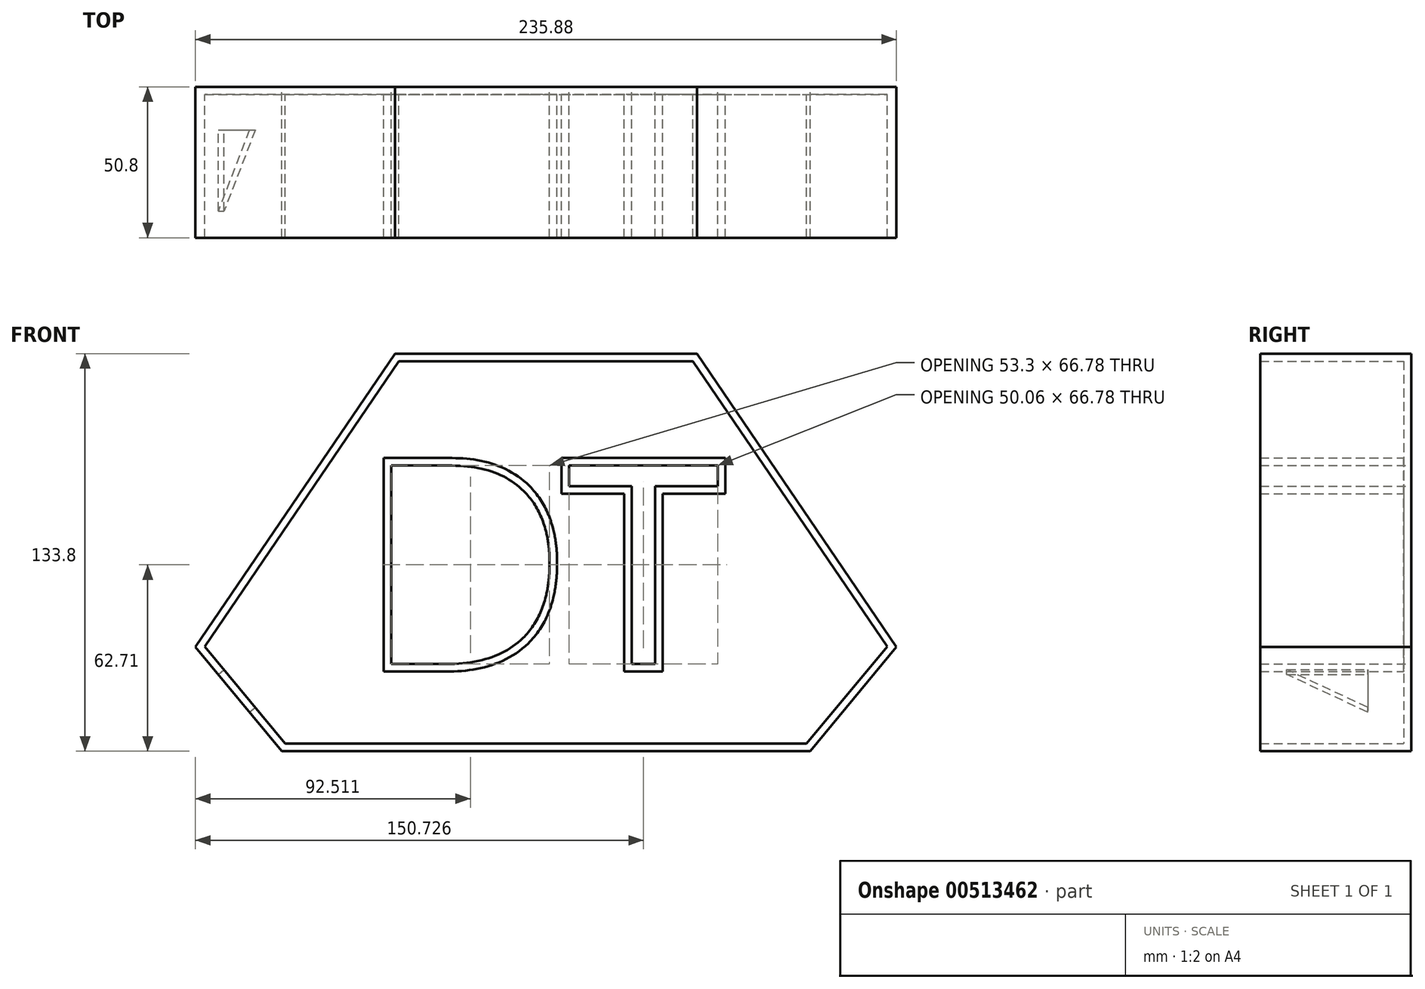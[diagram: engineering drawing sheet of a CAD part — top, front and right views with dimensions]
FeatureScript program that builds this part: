
annotation { "Feature Type Name" : "Feature", "Feature Type Description" : "" }
export const myFeature = defineFeature(function(context is Context, id is Id, definition is map)
    precondition{}
    {
        {
            var Q0;
            Q0=qCreatedBy(makeId("Front.planeOp"),FACE);
            var sketch = newSketch(context, id + "F0", { "sketchPlane" : qUnion([Q0])});
            skPoint(sketch, "E0.visualSharp", {"position": v(60.06, -91.32) * mm});
            skLineSegment(sketch, "E1", {"start": v(0, 83.88) * mm, "end": v(-50.8, 83.88) * mm});
            skLineSegment(sketch, "E2", {"start": v(-50.8, 83.88) * mm, "end": v(-117.94, -14.83) * mm});
            skLineSegment(sketch, "E3", {"start": v(-117.94, -14.83) * mm, "end": v(-88.9, -49.92) * mm});
            skLineSegment(sketch, "E4", {"start": v(-88.9, -49.92) * mm, "end": v(0, -49.92) * mm});
            skLineSegment(sketch, "E5.MirrorCS", {"start": v(0, 83.88) * mm, "end": v(50.8, 83.88) * mm});
            skLineSegment(sketch, "E6.MirrorCS", {"start": v(50.8, 83.88) * mm, "end": v(117.94, -14.83) * mm});
            skLineSegment(sketch, "E7.MirrorCS", {"start": v(117.94, -14.83) * mm, "end": v(88.9, -49.92) * mm});
            skLineSegment(sketch, "E8.MirrorCS", {"start": v(88.9, -49.92) * mm, "end": v(0, -49.92) * mm});
            skLineSegment(sketch, "E9", {"start": v(0, 83.88) * mm, "end": v(0, -49.92) * mm});
            skPoint(sketch, "E10.start.orphan", {"position": v(30.5, 62.6) * mm});
            skPoint(sketch, "E11.orphan", {"position": v(11.21, 62.6) * mm});
            skPoint(sketch, "E12.end.orphan", {"position": v(49.78, 62.6) * mm});
            skPoint(sketch, "E13.start.orphan", {"position": v(-50.8, 62.6) * mm});
            skPoint(sketch, "E14.end.orphan", {"position": v(11.21, -23.17) * mm});
            skText(sketch, "E15", { "text": "DT\n", "fontName": "OpenSans-Regular.ttf"});
            const initialGuessF0  = {"E15": [-0.06126, -0.0206, 1, 0, 0.06735]};
            skSetInitialGuess(sketch, initialGuessF0);
            skSolve(sketch);
        }
        {
            var Q0;
            {var subQ4=sQuery(id+"F0.wireOp",EDGE,"E1");Q0=makeQuery(id+"F0.imprint","IMPRINT",FACE,{"disambiguationData":[TD([[makeQuery(id+"F0.imprint","IMPRINT",EDGE,{"derivedFrom":subQ4}),1.0]])]});}
            var Q1;
            {var subQ7=sQuery(id+"F0.wireOp",EDGE,"E5.MirrorCS");Q1=makeQuery(id+"F0.imprint","IMPRINT",FACE,{"disambiguationData":[TD([[makeQuery(id+"F0.imprint","IMPRINT",EDGE,{"derivedFrom":subQ7}),-1.0]])]});}
            extrude(context, id + "F1", {"entities" : qUnion([Q0, Q1]), "depth" : 50.8 * mm});
        }
        {
            var Q0;
            Q0=makeQuery(id+"F1.opExtrude","CAP_FACE",FACE,{"disambiguationData":[OSD([sQuery(id+"F0.wireOp",EDGE,"E1"),sQuery(id+"F0.wireOp",EDGE,"E2"),sQuery(id+"F0.wireOp",EDGE,"E3"),sQuery(id+"F0.wireOp",EDGE,"E4"),sQuery(id+"F0.wireOp",EDGE,"E5.MirrorCS"),sQuery(id+"F0.wireOp",EDGE,"E6.MirrorCS"),sQuery(id+"F0.wireOp",EDGE,"E7.MirrorCS"),sQuery(id+"F0.wireOp",EDGE,"E8.MirrorCS"),sQuery(id+"F0.wireOp",EDGE,"E15.sketch_text.stroke-0"),sQuery(id+"F0.wireOp",EDGE,"E15.sketch_text.stroke-1"),sQuery(id+"F0.wireOp",EDGE,"E15.sketch_text.stroke-2"),sQuery(id+"F0.wireOp",EDGE,"E15.sketch_text.stroke-3"),sQuery(id+"F0.wireOp",EDGE,"E15.sketch_text.stroke-4"),sQuery(id+"F0.wireOp",EDGE,"E15.sketch_text.stroke-5"),sQuery(id+"F0.wireOp",EDGE,"E15.sketch_text.stroke-6"),sQuery(id+"F0.wireOp",EDGE,"E15.sketch_text.stroke-14"),sQuery(id+"F0.wireOp",EDGE,"E15.sketch_text.stroke-15"),sQuery(id+"F0.wireOp",EDGE,"E15.sketch_text.stroke-16"),sQuery(id+"F0.wireOp",EDGE,"E15.sketch_text.stroke-17"),sQuery(id+"F0.wireOp",EDGE,"E15.sketch_text.stroke-18"),sQuery(id+"F0.wireOp",EDGE,"E15.sketch_text.stroke-19"),sQuery(id+"F0.wireOp",EDGE,"E15.sketch_text.stroke-20"),sQuery(id+"F0.wireOp",EDGE,"E15.sketch_text.stroke-21")])],"isStart":false});
            shell(context, id + "F2", {"entities" : qUnion([Q0]), "thickness" : 2.54 * mm});
        }
        {
            var Q0;
            Q0=makeQuery(id+"F2.opShell","OFFSET_FACE",FACE,{"disambiguationData":[OSD([sQuery(id+"F0.wireOp",EDGE,"E3")])]});
            var sketch = newSketch(context, id + "F3", { "sketchPlane" : qUnion([Q0])});
            skLineSegment(sketch, "E16", {"start": v(-41.81, 51.7) * mm, "end": v(-14.57, 51.7) * mm});
            skLineSegment(sketch, "E17", {"start": v(-14.57, 51.7) * mm, "end": v(-14.57, 35.25) * mm});
            skLineSegment(sketch, "E18", {"start": v(-14.57, 35.25) * mm, "end": v(-41.81, 51.7) * mm});
            skSolve(sketch);
        }
        {
            var Q0;
            Q0=makeQuery(id+"F3.imprint","IMPRINT",FACE,{"disambiguationData":[TD([[makeQuery(id+"F3.imprint","IMPRINT",EDGE,{"derivedFrom":sQuery(id+"F3.wireOp",EDGE,"E16")}),-1.0]])]});
            extrude(context, id + "F4", {"entities" : qUnion([Q0]), "operationType" : NewBodyOperationType.REMOVE, "oppositeDirection" : true, "depth" : 127 * mm, "offsetDistance" : 25.4 * mm});
        }
    });
